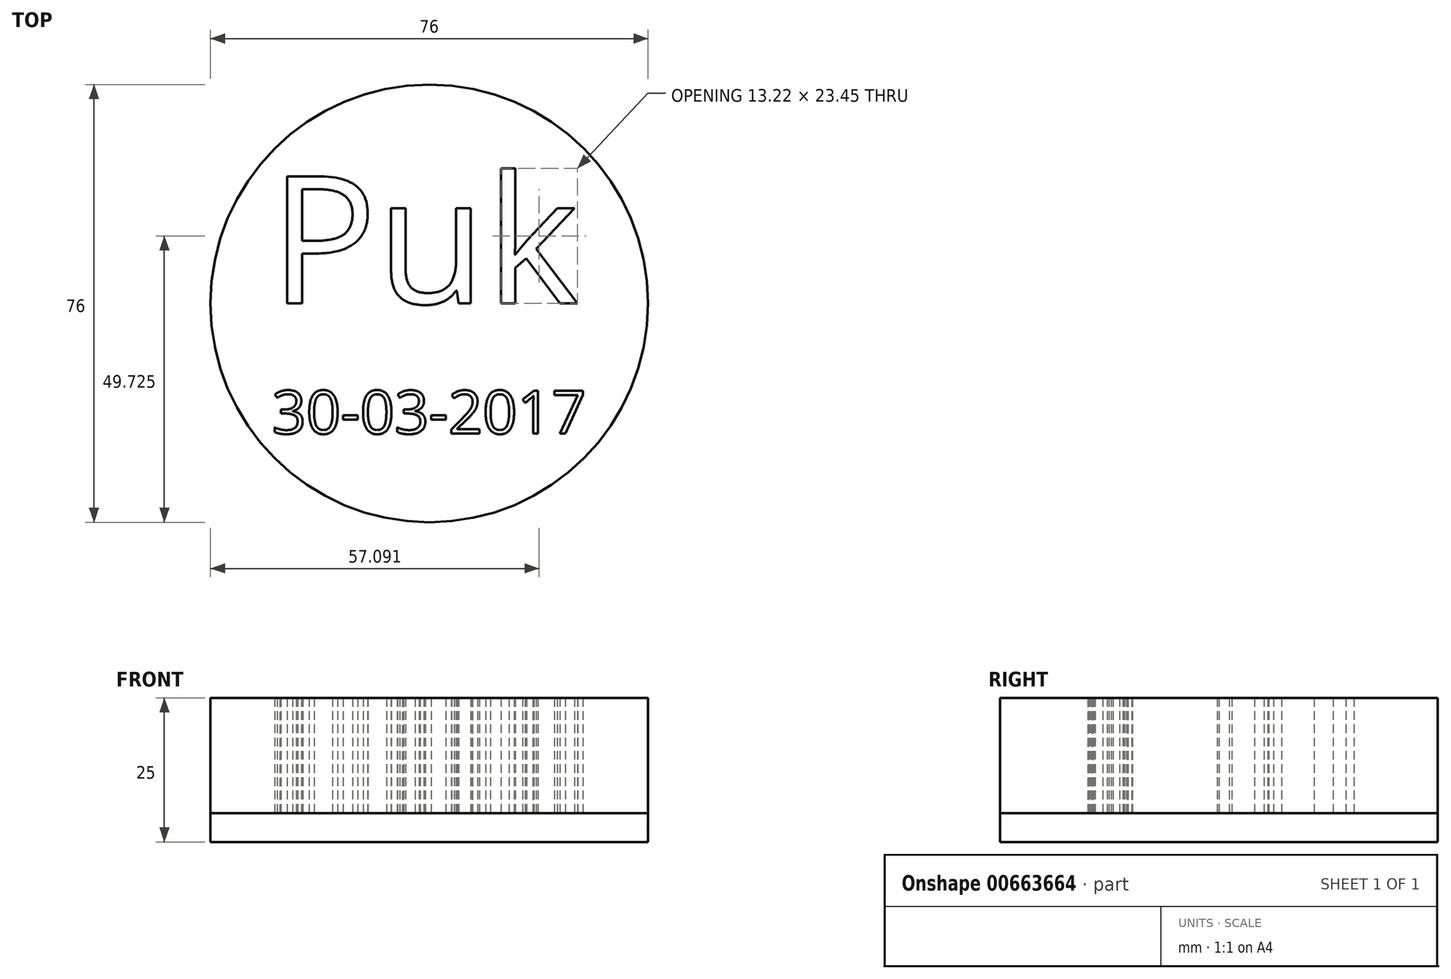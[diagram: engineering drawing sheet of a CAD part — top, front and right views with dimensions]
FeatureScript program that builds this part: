
annotation { "Feature Type Name" : "Feature", "Feature Type Description" : "" }
export const myFeature = defineFeature(function(context is Context, id is Id, definition is map)
    precondition{}
    {
        {
            var Q0;
            Q0=qCreatedBy(makeId("Top.planeOp"),FACE);
            var sketch = newSketch(context, id + "F0", { "sketchPlane" : qUnion([Q0])});
            skCircle(sketch, "E0", {"center": v(0, 0) * mm, "radius": 38 * mm});
            skText(sketch, "E1", { "text": "Puk", "fontName": "OpenSans-Regular.ttf"});
            skText(sketch, "E2", { "text": "30-03-2017", "fontName": "OpenSans-Regular.ttf"});
            const initialGuessF0  = {"E1": [-0.02769, 0, 1, 0, 0.02222], "E2": [-0.02736, -0.02262, 1, 0, 0.00753]};
            skSetInitialGuess(sketch, initialGuessF0);
            skSolve(sketch);
        }
        {
            var Q0;
            Q0 = qSketchRegion(id + "F0", true);
            extrude(context, id + "F1", {"entities" : qUnion([Q0]), "depth" : 20 * mm, "offsetDistance" : 25 * mm});
        }
        {
            var Q0;
            Q0=makeQuery(id+"F0.imprint","IMPRINT",FACE,{"disambiguationData":[TD([[makeQuery(id+"F0.imprint","IMPRINT",EDGE,{"derivedFrom":sQuery(id+"F0.wireOp",EDGE,"E1.sketch_text.stroke-8")}),1.0]])]});
            var Q1;
            Q1=makeQuery(id+"F0.imprint","IMPRINT",FACE,{"disambiguationData":[TD([[makeQuery(id+"F0.imprint","IMPRINT",EDGE,{"derivedFrom":sQuery(id+"F0.wireOp",EDGE,"E2.sketch_text.stroke-36")}),1.0]])]});
            var Q2;
            Q2=makeQuery(id+"F0.imprint","IMPRINT",FACE,{"disambiguationData":[TD([[makeQuery(id+"F0.imprint","IMPRINT",EDGE,{"derivedFrom":sQuery(id+"F0.wireOp",EDGE,"E2.sketch_text.stroke-56")}),1.0]])]});
            var Q3;
            Q3=makeQuery(id+"F0.imprint","IMPRINT",FACE,{"disambiguationData":[TD([[makeQuery(id+"F0.imprint","IMPRINT",EDGE,{"derivedFrom":sQuery(id+"F0.wireOp",EDGE,"E2.sketch_text.stroke-124")}),1.0]])]});
            extrude(context, id + "F2", {"entities" : qUnion([Q0, Q1, Q2, Q3]), "depth" : 20 * mm, "offsetDistance" : 25 * mm});
        }
        {
            var Q0;
            Q0=makeQuery(id+"F0.imprint","IMPRINT",FACE,{"disambiguationData":[TD([[makeQuery(id+"F0.imprint","IMPRINT",EDGE,{"derivedFrom":sQuery(id+"F0.wireOp",EDGE,"E0")}),1.0]])]});
            var sketch = newSketch(context, id + "F3", { "sketchPlane" : qUnion([Q0])});
            skCircle(sketch, "E3", {"center": v(0, 0) * mm, "radius": 38 * mm});
            skSolve(sketch);
        }
        {
            var Q0;
            Q0 = qSketchRegion(id + "F3", true);
            extrude(context, id + "F4", {"entities" : qUnion([Q0]), "oppositeDirection" : true, "depth" : 5 * mm, "offsetDistance" : 25 * mm});
        }
    });
